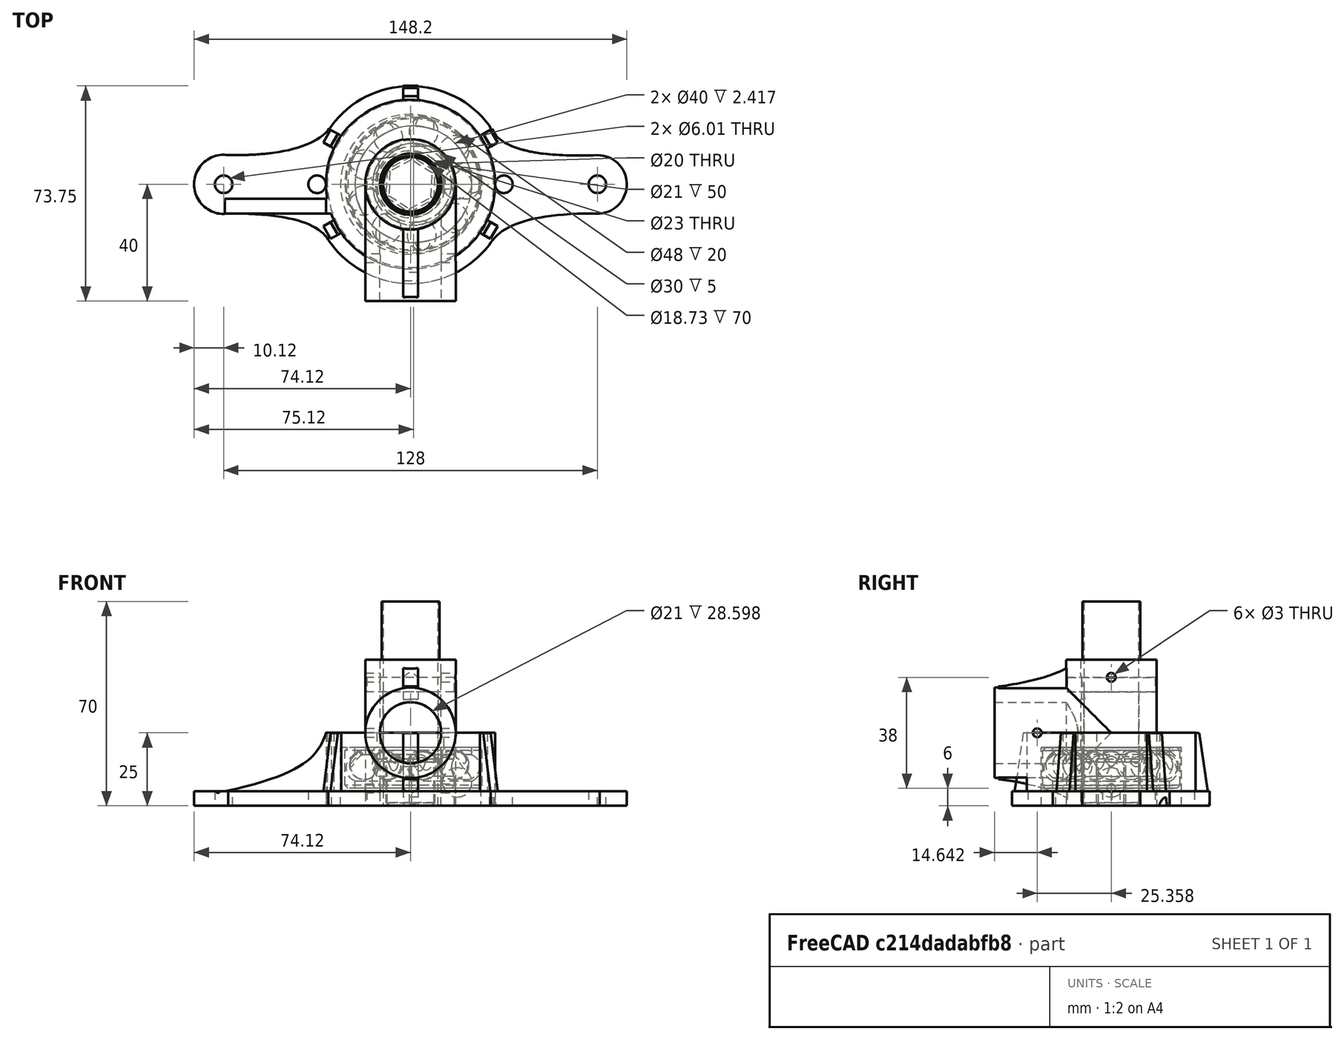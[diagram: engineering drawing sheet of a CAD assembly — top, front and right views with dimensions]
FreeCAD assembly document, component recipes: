
FREECAD ASSEMBLY — COMPONENT RECIPES ("dressingAutomatique")

This assembly document has 6 components, labeled P0..P5 below (a component is one placed body or linked part). 6 of them carry a construction recipe — the FreeCAD feature program that regenerates the part from scratch, quoted from this document or its linked companion documents; the rest are supplied as boundary geometry only. No exploded tour is included for this assembly.
COMPONENT P0 — recipe-attached ("Axe001", modeled in this document).
Construction recipe (the document's own serialized feature program — sketch geometry with constraints, then the solid features built on it; lengths are millimeters unless a unit is written):

FEATURE [Sketcher::SketchObject] Sketch004  label="axe"
  ArcFitTolerance = 1e-06
  AttachmentSupport = -> [XY_Plane001]
  FullyConstrained = true
  MakeInternals = false
  MapMode = 5
  sketch-geometry (2):
    g0: Circle CenterX=0 CenterY=0 CenterZ=0 NormalX=0 NormalY=0 NormalZ=1 AngleXU=0 Radius=15
    g1: Circle CenterX=0 CenterY=0 CenterZ=0 NormalX=0 NormalY=0 NormalZ=1 AngleXU=0 Radius=9.5
  constraints (4):
    c: Coincident(g0,g-1)
    c: Diameter(g0) = 30
    c: Coincident(g1,g0)
    c: Diameter(g1) = 19
FEATURE [PartDesign::Pad] Pad004  label="bute axe"
  Direction = (0,0,1)
  Length = 44
  Length2 = 10
  Profile = -> Sketch004 [Edge1]
  ReferenceAxis = -> Sketch004 [N_Axis]
  Suppressed = false
  Type = 0
FEATURE [PartDesign::Pocket] Pocket001  label="axe001"
  BaseFeature = -> Pad004
  Direction = (0,0,-1)
  Length = 39
  Length2 = 5
  Profile = -> Sketch004
  ReferenceAxis = -> Sketch004 [N_Axis]
  Reversed = true
  Suppressed = false
  Type = 0
FEATURE [Sketcher::SketchObject] Sketch005  label="hexa"
  ArcFitTolerance = 1e-06
  AttachmentSupport = -> [XY_Plane001]
  ExternalGeometry = -> [Sketch004]
  FullyConstrained = false
  MakeInternals = false
  MapMode = 5
  sketch-geometry (8):
    g0: LineSegment StartX=8.03876 StartY=-5.06244 StartZ=0 EndX=8.40359 EndY=4.43055 EndZ=0
    g1: LineSegment StartX=8.40359 StartY=4.43055 StartZ=0 EndX=0.364825 EndY=9.49299 EndZ=0
    g2: LineSegment StartX=0.364825 StartY=9.49299 StartZ=0 EndX=-8.03876 EndY=5.06244 EndZ=0
    g3: LineSegment StartX=-8.03876 StartY=5.06244 StartZ=0 EndX=-8.40359 EndY=-4.43055 EndZ=0
    g4: LineSegment StartX=-8.40359 StartY=-4.43055 StartZ=0 EndX=-0.364825 EndY=-9.49299 EndZ=0
    g5: LineSegment StartX=-0.364825 StartY=-9.49299 StartZ=0 EndX=8.03876 EndY=-5.06244 EndZ=0
    g6: Circle [constr] CenterX=0 CenterY=0 CenterZ=0 NormalX=0 NormalY=0 NormalZ=1 AngleXU=0 Radius=9.5
    g7: Circle CenterX=0 CenterY=0 CenterZ=0 NormalX=0 NormalY=0 NormalZ=1 AngleXU=0 Radius=12.1402
  constraints (16):
    c: Coincident(g0,g1)
    c: Coincident(g1,g2)
    c: Coincident(g2,g3)
    c: Coincident(g3,g4)
    c: Coincident(g4,g5)
    c: Coincident(g5,g0)
    c: Equal(g0, g1-g5) x5
    c: PointOnObject(g0,g6)
    c: PointOnObject(g1,g6)
    c: PointOnObject(g2,g6)
    c: PointOnObject(g3,g6)
    c: PointOnObject(g4,g6)
    c: PointOnObject(g5,g6)
    c: Coincident(g6,g-1)
    c: PointOnObject(g5,g-3)
    c: Coincident(g7,g6)
FEATURE [PartDesign::Pocket] Pocket002
  BaseFeature = -> Pocket001
  Direction = (0,0,-1)
  Length = 15
  Length2 = 5
  Profile = -> Sketch005
  ReferenceAxis = -> Sketch005 [N_Axis]
  Reversed = true
  Suppressed = false
  Type = 0
FEATURE [PartDesign::Chamfer] Chamfer
  Angle = 45
  Base = -> Pocket002 [Edge25,Edge23,Edge21,Edge30,Face17,Edge27]
  BaseFeature = -> Pocket002
  ChamferType = 0
  FlipDirection = false
  Size = 1
  Size2 = 1
  SupportTransform = false
  Suppressed = false
  UseAllEdges = false
FEATURE [PartDesign::Body] Body001  label="Axe"
  AllowCompound = false
  Group = -> [Sketch004,Pad004,Pocket001,Sketch005,Pocket002,Chamfer]
  Origin = -> Origin001
  Tip = -> Chamfer
COMPONENT P1 — recipe-attached ("Axe simple001", modeled in this document).
Construction recipe (the document's own serialized feature program — sketch geometry with constraints, then the solid features built on it; lengths are millimeters unless a unit is written):

FEATURE [Sketcher::SketchObject] Sketch016
  ArcFitTolerance = 1e-06
  AttachmentSupport = -> [XY_Plane006]
  FullyConstrained = false
  MakeInternals = false
  MapMode = 5
  sketch-geometry (2):
    g0: Circle CenterX=0 CenterY=0 CenterZ=0 NormalX=0 NormalY=0 NormalZ=1 AngleXU=0 Radius=9.90136
    g1: Circle CenterX=0 CenterY=0 CenterZ=0 NormalX=0 NormalY=0 NormalZ=1 AngleXU=0 Radius=9.36508
  constraints (2):
    c: Coincident(g0,g-1)
    c: Coincident(g1,g0)
FEATURE [PartDesign::Pad] Pad010
  Direction = (0,0,1)
  Length = 70
  Length2 = 10
  Profile = -> Sketch016
  ReferenceAxis = -> Sketch016 [N_Axis]
  Suppressed = false
  Type = 0
FEATURE [PartDesign::Body] Body005  label="Axe simple"
  AllowCompound = false
  Group = -> [Sketch016,Pad010]
  Origin = -> Origin006
  Tip = -> Pad010
COMPONENT P2 — recipe-attached ("Bouchon001", modeled in this document).
Construction recipe (the document's own serialized feature program — sketch geometry with constraints, then the solid features built on it; lengths are millimeters unless a unit is written):

FEATURE [Sketcher::SketchObject] Sketch009
  ArcFitTolerance = 1e-06
  AttachmentSupport = -> [XY_Plane004]
  FullyConstrained = true
  MakeInternals = false
  MapMode = 5
  sketch-geometry (2):
    g0: Circle CenterX=0 CenterY=0 CenterZ=0 NormalX=0 NormalY=0 NormalZ=1 AngleXU=0 Radius=28.5
    g1: Circle CenterX=0 CenterY=0 CenterZ=0 NormalX=0 NormalY=0 NormalZ=1 AngleXU=0 Radius=15
  constraints (4):
    c: Coincident(g0,g-1)
    c: Coincident(g1,g0)
    c: Diameter(g0) = 57
    c: Diameter(g1) = 30
FEATURE [PartDesign::Pad] Pad006
  Direction = (0,0,1)
  Length = 5
  Length2 = 10
  Profile = -> Sketch009
  ReferenceAxis = -> Sketch009 [N_Axis]
  Suppressed = false
  Type = 0
FEATURE [Sketcher::SketchObject] Sketch010
  ArcFitTolerance = 1e-06
  AttachmentSupport = -> [XY_Plane004]
  FullyConstrained = true
  MakeInternals = false
  MapMode = 5
  sketch-geometry (1):
    g0: Circle CenterX=0 CenterY=0 CenterZ=0 NormalX=0 NormalY=0 NormalZ=1 AngleXU=0 Radius=23.5
  constraints (2):
    c: Coincident(g0,g-1)
    c: Diameter(g0) = 47
FEATURE [PartDesign::Pocket] Pocket004
  BaseFeature = -> Pad006
  Direction = (0,0,-1)
  Length = 2
  Length2 = 5
  Profile = -> Sketch010
  ReferenceAxis = -> Sketch010 [N_Axis]
  Suppressed = false
  Type = 0
FEATURE [PartDesign::Body] Body003  label="Bouchon"
  AllowCompound = false
  Group = -> [Sketch009,Pad006,Sketch010,Pocket004]
  Origin = -> Origin004
  Tip = -> Pocket004
COMPONENT P3 — recipe-attached ("Roulement001", modeled in this document).
Construction recipe (the document's own serialized feature program — sketch geometry with constraints, then the solid features built on it; lengths are millimeters unless a unit is written):

FEATURE [PartDesign::FeatureBase] BaseFeature
  BaseFeature = -> Connect
  Suppressed = false
FEATURE [PartDesign::Body] Body002  label="Roulement"
  AllowCompound = false
  BaseFeature = -> Connect
  Group = -> [BaseFeature]
  Origin = -> Origin003
  Placement = pos=(0.999972,4.76837e-06,6.00003) rot=(0,0,1;0rad)
  Tip = -> BaseFeature
COMPONENT P4 — recipe-attached ("Support mur001", modeled in this document).
Construction recipe (the document's own serialized feature program — sketch geometry with constraints, then the solid features built on it; lengths are millimeters unless a unit is written):

FEATURE [Sketcher::SketchObject] Sketch  label="roulement"
  ArcFitTolerance = 1e-06
  AttachmentSupport = -> [XY_Plane]
  FullyConstrained = true
  MakeInternals = false
  MapMode = 5
  sketch-geometry (2):
    g0: Circle CenterX=0 CenterY=0 CenterZ=0 NormalX=0 NormalY=0 NormalZ=1 AngleXU=0 Radius=11.5
    g1: Circle CenterX=0 CenterY=0 CenterZ=0 NormalX=0 NormalY=0 NormalZ=1 AngleXU=0 Radius=29
  constraints (4):
    c: Coincident(g0,g-1)
    c: Diameter(g0) = 23
    c: Coincident(g1,g0)
    c: Diameter(g1) = 58
FEATURE [Sketcher::SketchObject] Sketch001  label="platine"
  ArcFitTolerance = 1e-06
  AttachmentSupport = -> [XY_Plane]
  FullyConstrained = false
  MakeInternals = false
  MapMode = 5
  sketch-geometry (42):
    g0: LineSegment [constr] StartX=-64.5 StartY=34 StartZ=0 EndX=-64.5 EndY=-34 EndZ=0
    g1: LineSegment [constr] StartX=-64.5 StartY=-34 StartZ=0 EndX=64.5 EndY=-34 EndZ=0
    g2: LineSegment [constr] StartX=64.5 StartY=-34 StartZ=0 EndX=64.5 EndY=34 EndZ=0
    g3: LineSegment [constr] StartX=64.5 StartY=34 StartZ=0 EndX=-64.5 EndY=34 EndZ=0
    g4: GeomPoint [constr] X=47.479 Y=17.6674 Z=0
    g5: ArcOfCircle CenterX=0 CenterY=0 CenterZ=0 NormalX=0 NormalY=0 NormalZ=1 AngleXU=0 Radius=34 StartAngle=3.73456 EndAngle=5.65431
    g6: Circle [constr] CenterX=-62.443 CenterY=-10 CenterZ=0 NormalX=0 NormalY=0 NormalZ=1 AngleXU=0 Radius=1
    g7: Circle [constr] CenterX=-33.5653 CenterY=-9.84859 CenterZ=0 NormalX=0 NormalY=0 NormalZ=1 AngleXU=0 Radius=1
    g8: Circle [constr] CenterX=-28.1957 CenterY=-19 CenterZ=0 NormalX=0 NormalY=0 NormalZ=1 AngleXU=0 Radius=1
    g9: BSplineCurve PolesCount=3 KnotsCount=2 Degree=2 IsPeriodic=0
    g10: GeomPoint [constr] X=-62.443 Y=-10 Z=0
    g11: GeomPoint [constr] X=-28.1957 Y=-19 Z=0
    g12: LineSegment [constr] StartX=-139.75 StartY=-10 StartZ=0 EndX=108.432 EndY=-10 EndZ=0
    g13: LineSegment [constr] StartX=-56.9057 StartY=-20 StartZ=0 EndX=73.6028 EndY=-20 EndZ=0
    g14: ArcOfCircle CenterX=-64 CenterY=0 CenterZ=0 NormalX=0 NormalY=0 NormalZ=1 AngleXU=0 Radius=10.1205 StartAngle=1.41634 EndAngle=4.86685
    g15: BSplineCurve PolesCount=3 KnotsCount=2 Degree=2 IsPeriodic=0
    g16: Circle [constr] CenterX=-62.443 CenterY=10 CenterZ=0 NormalX=0 NormalY=0 NormalZ=1 AngleXU=0 Radius=1
    g17: Circle [constr] CenterX=-33.9289 CenterY=9.66678 CenterZ=0 NormalX=0 NormalY=0 NormalZ=1 AngleXU=0 Radius=1
    g18: Circle [constr] CenterX=-27.0839 CenterY=20.0395 CenterZ=0 NormalX=0 NormalY=0 NormalZ=1 AngleXU=0 Radius=1
    g19: GeomPoint [constr] X=-62.443 Y=10 Z=0
    g20: GeomPoint [constr] X=-27.0839 Y=20.0395 Z=0
    g21: ArcOfCircle CenterX=0 CenterY=0 CenterZ=0 NormalX=0 NormalY=0 NormalZ=1 AngleXU=0 Radius=33.6915 StartAngle=0.637008 EndAngle=2.50458
    g22: ArcOfCircle CenterX=64.071 CenterY=-0.013204 CenterZ=0 NormalX=0 NormalY=0 NormalZ=1 AngleXU=0 Radius=10.0132 StartAngle=4.78503 EndAngle=7.85398
    g23: BSplineCurve PolesCount=3 KnotsCount=2 Degree=2 IsPeriodic=0
    g24: BSplineCurve PolesCount=3 KnotsCount=2 Degree=2 IsPeriodic=0
    g25: Circle [constr] CenterX=64.071 CenterY=10 CenterZ=0 NormalX=0 NormalY=0 NormalZ=1 AngleXU=0 Radius=1
    g26: Circle [constr] CenterX=31.305 CenterY=8.64637 CenterZ=0 NormalX=0 NormalY=0 NormalZ=1 AngleXU=0 Radius=1
    g27: Circle [constr] CenterX=27.0839 CenterY=20.0395 CenterZ=0 NormalX=0 NormalY=0 NormalZ=1 AngleXU=0 Radius=1
    g28: GeomPoint [constr] X=64.071 Y=10 Z=0
    g29: GeomPoint [constr] X=27.0839 Y=20.0395 Z=0
    g30: Circle [constr] CenterX=64.7978 CenterY=-10 CenterZ=0 NormalX=0 NormalY=0 NormalZ=1 AngleXU=0 Radius=1
    g31: Circle [constr] CenterX=33.9289 CenterY=-9.66678 CenterZ=0 NormalX=0 NormalY=0 NormalZ=1 AngleXU=0 Radius=1
    g32: Circle [constr] CenterX=27.4955 CenterY=-20 CenterZ=0 NormalX=0 NormalY=0 NormalZ=1 AngleXU=0 Radius=1
    g33: GeomPoint [constr] X=64.7978 Y=-10 Z=0
    g34: GeomPoint [constr] X=27.4955 Y=-20 Z=0
    g35: LineSegment [constr] StartX=-146.84 StartY=10 StartZ=0 EndX=88.6661 EndY=10 EndZ=0
    g36: LineSegment [constr] StartX=-56.9057 StartY=20.0395 StartZ=0 EndX=73.6028 EndY=20.0395 EndZ=0
    g37: Circle CenterX=-32 CenterY=0 CenterZ=0 NormalX=0 NormalY=0 NormalZ=1 AngleXU=0 Radius=3.00257
    g38: Circle CenterX=0 CenterY=0 CenterZ=0 NormalX=0 NormalY=0 NormalZ=1 AngleXU=0 Radius=3.00257
    g39: Circle CenterX=32 CenterY=0 CenterZ=0 NormalX=0 NormalY=0 NormalZ=1 AngleXU=0 Radius=3.00257
    g40: Circle CenterX=-64 CenterY=0 CenterZ=0 NormalX=0 NormalY=0 NormalZ=1 AngleXU=0 Radius=3.005
    g41: Circle CenterX=64 CenterY=0 CenterZ=0 NormalX=0 NormalY=0 NormalZ=1 AngleXU=0 Radius=3.00257
  constraints (71):
    c: Coincident(g0,g1)
    c: Coincident(g1,g2)
    c: Coincident(g2,g3)
    c: Coincident(g3,g0)
    c: Vertical(g0)
    c: Horizontal(g1)
    c: DistanceY(g2,g2) = 68
    c: DistanceX(g1,g1) = 129
    c: Symmetric(g2,g1,g-1)
    c: Symmetric(g2,g0,g-2)
    c: Weight(g6) = 1
    c: Equal(g6,g7)
    c: Equal(g6,g8)
    c: InternalAlignment(g6,g9)
    c: InternalAlignment(g7,g9)
    c: InternalAlignment(g8,g9)
    c: InternalAlignment(g10,g9)
    c: InternalAlignment(g11,g9)
    c: Coincident(g8,g5)
    c: Horizontal(g12)
    c: Distance(g12,g-1) = 10
    c: Horizontal(g13)
    c: Tangent(g13,g8)
    c: Distance(g13,g-1) = 20
    c: PointOnObject(g5,g13)
    c: Tangent(g5,g1)
    c: Weight(g16) = 1
    c: Equal(g16,g17)
    c: Equal(g16,g18)
    c: InternalAlignment(g16-g20 -> g15) x5
    c: Coincident(g16,g14)
    c: Coincident(g21,g15)
    c: Coincident(g14,g9)
    c: Weight(g30) = 1
    c: Equal(g30,g31)
    c: Equal(g30,g32)
    c: InternalAlignment(g30-g34 -> g24) x5
    c: Weight(g25) = 1
    c: Equal(g25,g26)
    c: Equal(g25,g27)
    c: InternalAlignment(g25-g29 -> g23) x5
    c: Coincident(g25,g22)
    c: Coincident(g22,g24)
    c: Coincident(g24,g5)
    c: Coincident(g23,g21)
    c: PointOnObject(g14,g-1)
    c: PointOnObject(g22,g12)
    c: Horizontal(g35)
    c: Horizontal(g36)
    c: PointOnObject(g21,g36)
    c: PointOnObject(g15,g36)
    c: Diameter(g37) = 6.00515
    c: Diameter(g38) = 6.00515
    c: Diameter(g39) = 6.00515
    c: Coincident(g-1,g5)
    c: Coincident(g-1,g21)
    c: Coincident(g38,g5)
    c: PointOnObject(g37,g-1)
    c: PointOnObject(g39,g-1)
    c: DistanceX(g37,g5) = 32
    c: DistanceX(g5,g39) = 32
    c: PointOnObject(g23,g35)
    c: Diameter(g40) = 6.01
    c: DistanceX(g40,g37) = 32
    c: PointOnObject(g15,g35)
    c: PointOnObject(g9,g12)
    c: Diameter(g41) = 6.00515
    c: PointOnObject(g41,g-1)
    c: DistanceX(g39,g41) = 32
    c: Coincident(g14,g40)
    c: Distance(g35,g-1) = 10
FEATURE [Sketcher::SketchObject] Sketch003  label="renfprt"
  ArcFitTolerance = 1e-06
  AttachmentOffset = pos=(30,0,0) rot=(0,0,1;0rad)
  AttachmentSupport = -> [YZ_Plane]
  FullyConstrained = false
  MakeInternals = false
  MapMode = 5
  Placement = pos=(0,30,0) rot=(0.57735,0.57735,0.57735;2.0944rad)
  sketch-geometry (4):
    g0: LineSegment StartX=-2.07385 StartY=24.959 StartZ=0 EndX=-2.07385 EndY=0 EndZ=0
    g1: LineSegment StartX=-2.07385 StartY=0 StartZ=0 EndX=3.74646 EndY=0 EndZ=0
    g2: LineSegment StartX=-2.07385 StartY=24.959 StartZ=0 EndX=0.193659 EndY=24.959 EndZ=0
    g3: LineSegment StartX=0.193659 StartY=24.959 StartZ=0 EndX=3.74646 EndY=0 EndZ=0
  constraints (8):
    c: Coincident(g0,g1)
    c: Vertical(g0)
    c: Horizontal(g1)
    c: PointOnObject(g1,g-1)
    c: Coincident(g2,g0)
    c: Coincident(g3,g2)
    c: Coincident(g3,g1)
    c: Horizontal(g2)
FEATURE [Sketcher::SketchObject] Sketch006
  ArcFitTolerance = 1e-06
  AttachmentOffset = pos=(0,0,5) rot=(0,0,1;0rad)
  AttachmentSupport = -> [XZ_Plane]
  FullyConstrained = false
  MakeInternals = false
  MapMode = 5
  Placement = pos=(0,-5,1.1e-15) rot=(1,0,0;1.5708rad)
  sketch-geometry (11):
    g0: LineSegment StartX=-66.3753 StartY=4.44189 StartZ=0 EndX=-26.6331 EndY=4.44189 EndZ=0
    g1: LineSegment StartX=-26.6331 StartY=4.44189 StartZ=0 EndX=-26.6331 EndY=25 EndZ=0
    g2: GeomPoint [constr] X=-28.9519 Y=25 Z=0
    g3: GeomPoint [constr] X=-38.0241 Y=13.5983 Z=0
    g4: GeomPoint [constr] X=-66.3753 Y=4.44189 Z=0
    g5: BSplineCurve PolesCount=4 KnotsCount=2 Degree=3 IsPeriodic=0
    g6-g9: Circle [constr] x4 (B-spline internal-alignment scaffolding for g5; pole/knot coordinates omitted)
    g10: LineSegment StartX=-26.6331 StartY=25 StartZ=0 EndX=-28.9519 EndY=25 EndZ=0
  constraints (19):
    c: Vertical(g1)
    c: InternalAlignment(g2,g5)
    c: PointOnObject(g3,g5)
    c: InternalAlignment(g4,g5)
    c: InternalAlignment(g6,g5)
    c: Weight(g6) = 1
    c: InternalAlignment(g7,g5)
    c: Equal(g7,g6)
    c: InternalAlignment(g8,g5)
    c: Equal(g8,g6)
    c: InternalAlignment(g9,g5)
    c: Equal(g9,g6)
    c: Coincident(g1,g0)
    c: Coincident(g5,g0)
    c: Horizontal(g0)
    c: PointOnObject(g1,g-3)
    c: Coincident(g10,g1)
    c: PointOnObject(g10,g-3)
    c: Coincident(g5,g10)
FEATURE [PartDesign::LinearPattern] LinearPattern
  Direction = -> Y_Axis
  Length = 15
  Mode = 0
  Occurrences = 2
  Offset = 15
  Suppressed = false
  TransformMode = 0
FEATURE [PartDesign::PolarPattern] PolarPattern002
  Angle = 360
  Axis = -> Z_Axis
  Mode = 0
  Occurrences = 2
  Offset = 120
  Suppressed = false
  TransformMode = 0
FEATURE [Sketcher::SketchObject] Sketch007  label="roulement insert"
  ArcFitTolerance = 1e-06
  AttachmentSupport = -> [XY_Plane]
  FullyConstrained = true
  MakeInternals = false
  MapMode = 5
  sketch-geometry (1):
    g0: Circle CenterX=0 CenterY=0 CenterZ=0 NormalX=0 NormalY=0 NormalZ=1 AngleXU=0 Radius=24
  constraints (2):
    c: Coincident(g0,g-1)
    c: Radius(g0) = 24
FEATURE [PartDesign::Pad] Pad
  Direction = (0,0,1)
  Length = 25
  Length2 = 10
  Profile = -> Sketch
  ReferenceAxis = -> Sketch [N_Axis]
  Suppressed = false
  Type = 0
FEATURE [PartDesign::Pad] Pad001
  BaseFeature = -> Pad
  Direction = (0,0,1)
  Length = 5
  Length2 = 10
  Profile = -> Sketch001
  ReferenceAxis = -> Sketch001 [N_Axis]
  Suppressed = false
  Type = 0
FEATURE [PartDesign::Pocket] Pocket
  BaseFeature = -> Pad001
  Direction = (0,0,-1)
  Length = 20
  Length2 = 10
  Profile = -> Sketch007
  ReferenceAxis = -> Sketch007 [N_Axis]
  Reversed = true
  Suppressed = false
  Type = 4
FEATURE [PartDesign::Pad] Pad003  label="renfort roulement"
  BaseFeature = -> Pocket
  Direction = (1,0,0)
  Length = 2.5
  Length2 = 2.5
  Profile = -> Sketch003
  ReferenceAxis = -> Sketch003 [N_Axis]
  Suppressed = false
  Type = 4
FEATURE [PartDesign::PolarPattern] PolarPattern
  Angle = 360
  Axis = -> Z_Axis
  BaseFeature = -> Pad003
  Mode = 0
  Occurrences = 6
  Offset = 120
  Originals = -> [Pad003]
  Suppressed = false
  TransformMode = 0
FEATURE [PartDesign::Pad] Pad005  label="renfort platine"
  BaseFeature = -> PolarPattern
  Direction = (0,-1,2e-16)
  Length = 5
  Length2 = 15
  Profile = -> Sketch006
  ReferenceAxis = -> Sketch006 [N_Axis]
  Suppressed = false
  Type = 0
FEATURE [PartDesign::MultiTransform] MultiTransform
  BaseFeature = -> Pad005
  Originals = -> [Pad005]
  Suppressed = false
  TransformMode = 0
  Transformations = -> [LinearPattern,PolarPattern002]
FEATURE [Sketcher::SketchObject] Sketch008
  ArcFitTolerance = 1e-06
  AttachmentOffset = pos=(0,0,5) rot=(0,0,1;0rad)
  AttachmentSupport = -> [XY_Plane]
  ExternalGeometry = -> [Sketch001]
  FullyConstrained = true
  MakeInternals = false
  MapMode = 5
  Placement = pos=(0,0,5) rot=(0,0,1;0rad)
  sketch-geometry (2):
    g0: Circle CenterX=-32 CenterY=0 CenterZ=0 NormalX=0 NormalY=0 NormalZ=1 AngleXU=0 Radius=4.5
    g1: Circle CenterX=32 CenterY=0 CenterZ=0 NormalX=0 NormalY=0 NormalZ=1 AngleXU=0 Radius=4.5
  constraints (4):
    c: Coincident(g0,g-3)
    c: Coincident(g1,g-4)
    c: Diameter(g0) = 9
    c: Diameter(g1) = 9
FEATURE [PartDesign::Pocket] Pocket003
  BaseFeature = -> MultiTransform
  Direction = (0,0,-1)
  Length = 28
  Length2 = 5
  Profile = -> Sketch008
  ReferenceAxis = -> Sketch008 [N_Axis]
  Reversed = true
  Suppressed = false
  Type = 0
FEATURE [PartDesign::Body] Body  label="Support mur"
  AllowCompound = false
  Group = -> [Pad,Pad001,Sketch,Pocket,Sketch001,Sketch003,Pad003,PolarPattern,Sketch006,Pad005,PolarPattern002,Sketch007,Sketch008,MultiTransform,Pocket003,LinearPattern]
  Origin = -> Origin
  Tip = -> Pad005
COMPONENT P5 — recipe-attached ("T001", modeled in this document).
Construction recipe (the document's own serialized feature program — sketch geometry with constraints, then the solid features built on it; lengths are millimeters unless a unit is written):

FEATURE [Sketcher::SketchObject] Sketch011
  ArcFitTolerance = 1e-06
  AttachmentSupport = -> [XY_Plane005]
  FullyConstrained = false
  MakeInternals = false
  MapMode = 5
  sketch-geometry (1):
    g0: Circle CenterX=0 CenterY=0 CenterZ=0 NormalX=0 NormalY=0 NormalZ=1 AngleXU=0 Radius=15.5
  constraints (1):
    c: Diameter(g0) = 31
FEATURE [Sketcher::SketchObject] Sketch012
  ArcFitTolerance = 1e-06
  AttachmentSupport = -> [XZ_Plane005]
  FullyConstrained = false
  MakeInternals = false
  MapMode = 5
  Placement = pos=(0,0,0) rot=(1,0,0;1.5708rad)
  sketch-geometry (2):
    g0: Circle CenterX=0 CenterY=25 CenterZ=0 NormalX=0 NormalY=0 NormalZ=1 AngleXU=0 Radius=15.5
    g1: Circle CenterX=0 CenterY=25 CenterZ=0 NormalX=0 NormalY=0 NormalZ=1 AngleXU=0 Radius=10.5
  constraints (4):
    c: Diameter(g0) = 31
    c: DistanceY(g-1,g0) = 25
    c: Coincident(g1,g0)
    c: Diameter(g1) = 21
FEATURE [PartDesign::Pad] Pad008
  Direction = (0,-1,2e-16)
  Length = 40
  Length2 = 10
  Placement = pos=(0,0,0) rot=(1,0,0;1.5708rad)
  Profile = -> Sketch012
  ReferenceAxis = -> Sketch012 [N_Axis]
  Suppressed = false
  Type = 0
FEATURE [PartDesign::Pad] Pad007
  BaseFeature = -> Pad008
  Direction = (0,0,1)
  Length = 50
  Length2 = 10
  Placement = pos=(0,0,0) rot=(1,0,0;1.5708rad)
  Profile = -> Sketch011
  ReferenceAxis = -> Sketch011 [N_Axis]
  Suppressed = false
  Type = 0
FEATURE [Sketcher::SketchObject] Sketch013
  ArcFitTolerance = 1e-06
  AttachmentSupport = -> [XY_Plane005]
  FullyConstrained = true
  MakeInternals = false
  MapMode = 5
  sketch-geometry (1):
    g0: Circle CenterX=0 CenterY=0 CenterZ=0 NormalX=0 NormalY=0 NormalZ=1 AngleXU=0 Radius=10.5
  constraints (2):
    c: Coincident(g0,g-1)
    c: Diameter(g0) = 21
FEATURE [PartDesign::Pocket] Pocket005
  BaseFeature = -> Pad007
  Direction = (0,0,-1)
  Length = 5
  Length2 = 5
  Placement = pos=(0,0,0) rot=(1,0,0;1.5708rad)
  Profile = -> Sketch013
  ReferenceAxis = -> Sketch013 [N_Axis]
  Reversed = true
  Suppressed = false
  Type = 1
FEATURE [Sketcher::SketchObject] Sketch014
  ArcFitTolerance = 1e-06
  AttachmentOffset = pos=(0,1.5,-2.5) rot=(0,0,1;0rad)
  AttachmentSupport = -> [YZ_Plane005]
  ExternalGeometry = -> [Sketch012]
  FullyConstrained = false
  MakeInternals = false
  MapMode = 5
  Placement = pos=(-2.5,0,1.5) rot=(0.57735,0.57735,0.57735;2.0944rad)
  sketch-geometry (10):
    g0: Circle [constr] CenterX=-38.6494 CenterY=39.3664 CenterZ=0 NormalX=0 NormalY=0 NormalZ=1 AngleXU=0 Radius=1
    g1: Circle [constr] CenterX=-19.1662 CenterY=41.8877 CenterZ=0 NormalX=0 NormalY=0 NormalZ=1 AngleXU=0 Radius=1
    g2: Circle [constr] CenterX=-11.1428 CenterY=48.3038 CenterZ=0 NormalX=0 NormalY=0 NormalZ=1 AngleXU=0 Radius=1
    g3: BSplineCurve PolesCount=3 KnotsCount=2 Degree=2 IsPeriodic=0
    g4: GeomPoint [constr] X=-38.6494 Y=39.3664 Z=0
    g5: GeomPoint [constr] X=-11.1428 Y=48.3038 Z=0
    g6: LineSegment StartX=-11.1428 StartY=48.3038 StartZ=0 EndX=-9.08077 EndY=35.0113 EndZ=0
    g7: LineSegment StartX=-9.08077 StartY=35.0113 StartZ=0 EndX=-38.8787 EndY=35.0113 EndZ=0
    g8: LineSegment StartX=-38.8787 StartY=35.0113 StartZ=0 EndX=-38.6494 EndY=39.3664 EndZ=0
    g9: LineSegment [constr] StartX=-43.4272 StartY=23.5 StartZ=0 EndX=46.883 EndY=23.5 EndZ=0
  constraints (14):
    c: Weight(g0) = 1
    c: Equal(g0,g1)
    c: Equal(g0,g2)
    c: InternalAlignment(g0,g3)
    c: InternalAlignment(g1,g3)
    c: InternalAlignment(g2,g3)
    c: InternalAlignment(g4,g3)
    c: InternalAlignment(g5,g3)
    c: Coincident(g6,g3)
    c: Coincident(g7,g6)
    c: Horizontal(g7)
    c: Coincident(g8,g7)
    c: Coincident(g8,g3)
    c: Symmetric(g-3,g-3,g9)
FEATURE [PartDesign::Pad] Pad009
  BaseFeature = -> Pocket005
  Direction = (1,0,0)
  Length = 5
  Length2 = 10
  Placement = pos=(0,0,0) rot=(1,0,0;1.5708rad)
  Profile = -> Sketch014
  ReferenceAxis = -> Sketch014 [N_Axis]
  Suppressed = false
  Type = 0
FEATURE [PartDesign::Mirrored] Mirrored
  BaseFeature = -> Pad009
  MirrorPlane = -> Sketch014 [Axis]
  Originals = -> [Pad009]
  Placement = pos=(0,0,0) rot=(1,0,0;1.5708rad)
  Suppressed = false
  TransformMode = 0
FEATURE [Sketcher::SketchObject] Sketch015
  ArcFitTolerance = 1e-06
  AttachmentSupport = -> [YZ_Plane005]
  FullyConstrained = false
  MakeInternals = false
  MapMode = 5
  Placement = pos=(0,0,0) rot=(0.57735,0.57735,0.57735;2.0944rad)
  sketch-geometry (4):
    g0: Circle CenterX=0 CenterY=6 CenterZ=0 NormalX=0 NormalY=0 NormalZ=1 AngleXU=0 Radius=1.5
    g1: Circle CenterX=0 CenterY=44 CenterZ=0 NormalX=0 NormalY=0 NormalZ=1 AngleXU=0 Radius=1.5
    g2: Circle CenterX=-25.3585 CenterY=25 CenterZ=0 NormalX=0 NormalY=0 NormalZ=1 AngleXU=0 Radius=1.5
    g3: LineSegment [constr] StartX=-47.1325 StartY=25 StartZ=0 EndX=65.8699 EndY=25 EndZ=0
  constraints (9):
    c: PointOnObject(g0,g-2)
    c: PointOnObject(g1,g-2)
    c: Diameter(g0) = 3
    c: Diameter(g1) = 3
    c: Distance(g0,g-1) = 6
    c: DistanceY(g-1,g1) = 44
    c: Diameter(g2) = 3
    c: Symmetric(g1,g0,g3)
    c: PointOnObject(g2,g3)
FEATURE [PartDesign::Pocket] Pocket006
  BaseFeature = -> Mirrored
  Direction = (-1,0,0)
  Length = 38
  Length2 = 30
  Placement = pos=(0,0,0) rot=(1,0,0;1.5708rad)
  Profile = -> Sketch015
  ReferenceAxis = -> Sketch015 [N_Axis]
  Reversed = true
  Suppressed = false
  Type = 4
FEATURE [PartDesign::Body] Body004  label="T"
  AllowCompound = false
  Group = -> [Sketch011,Sketch012,Pad008,Pad007,Sketch013,Pocket005,Sketch014,Pad009,Mirrored,Sketch015,Pocket006]
  Origin = -> Origin005
  Tip = -> Pocket006
PROVENANCE & LICENSES
A FreeCAD (.FCStd) document from a public repository crawl; recipes are the document's own serialized feature recipes (and, for linked parts, companion documents' recipes).
License: as declared in the source repository (recorded in the dataset sidecar).
